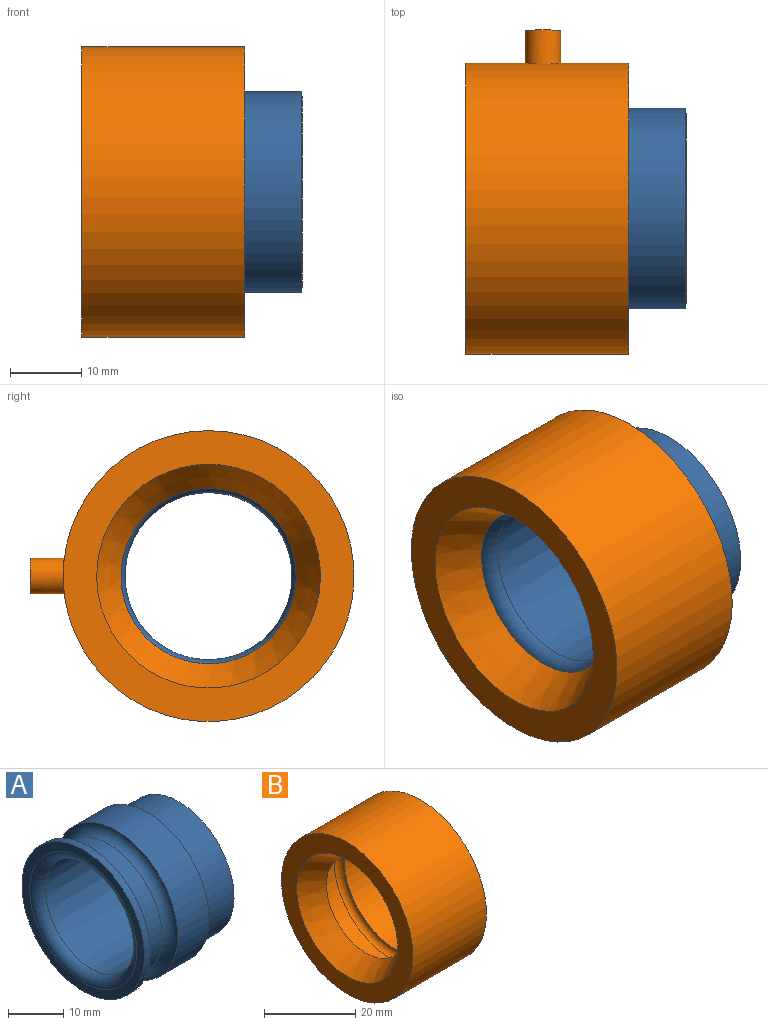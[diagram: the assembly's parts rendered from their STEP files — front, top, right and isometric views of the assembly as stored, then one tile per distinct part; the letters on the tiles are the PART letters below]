
ASSEMBLY  parts=2 mates=1
PART A: 12 faces, bbox 24.5x37x37 mm
  f0: plane 31.32x31.32mm, normal (-1,0,0), area 181mm2, adj f1,f11
  f1: torus R=13.7mm, axis (-1,0,0), area 248.4mm2, adj f0,f2
  f2: cone r=11.69mm half-angle=0.9deg, axis (1,0,0), area 1677mm2, adj f1,f3
  f3: cone r=12.04mm half-angle=89.1deg, axis (-1,0,0), area 164.6mm2, adj f2,f4
  f4: cylinder r=14.05mm len=28.09mm, axis (-1,0,0), area 706mm2, adj f3,f5
  f5: plane 31.32x31.32mm, normal (1,0,0), area 150.9mm2, adj f4,f6
  f6: cylinder r=15.66mm len=31.32mm, axis (-1,0,0), area 787.3mm2, adj f5,f7
  f7: torus R=15.66mm, axis (-1,0,0), area 284mm2, adj f6,f8
  f8: cylinder r=13.66mm len=27.32mm, axis (-1,0,0), area 343.4mm2, adj f7,f9
  f9: torus R=14.66mm, axis (-1,0,0), area 138.4mm2, adj f8,f10
  f10: plane 31.32x31.32mm, normal (1,0,0), area 95.3mm2, adj f9,f11
  f11: cylinder r=15.66mm len=31.32mm, axis (-1,0,0), area 147.6mm2, adj f0,f10
PART B: 13 faces, bbox 22.8x45.4x40.7 mm
  f0: cylinder r=17.37mm len=34.74mm, axis (-1,0,0), area 645.2mm2, adj f1,f9,f10
  f1: torus R=15.87mm, axis (-1,0,0), area 249.1mm2, adj f0,f2
  f2: plane 31.74x31.74mm, normal (-1,0,0), area 20.4mm2, adj f1,f3
  f3: cylinder r=15.66mm len=31.32mm, axis (-1,0,0), area 787.3mm2, adj f2,f4
  f4: plane 40.74x40.74mm, normal (1,0,0), area 532.7mm2, adj f3,f5
  f5: cylinder r=20.37mm len=40.74mm, axis (-1,0,0), area 2899.8mm2, adj f4,f6,f11
  f6: plane 40.74x40.74mm, normal (-1,0,0), area 532.7mm2, adj f5,f7
  f7: cone r=15.66mm half-angle=30.3deg, axis (-1,0,0), area 590.6mm2, adj f6,f8
  f8: plane 31.74x31.74mm, normal (1,0,0), area 318.3mm2, adj f7,f9
  f9: torus R=15.87mm, axis (-1,0,0), area 249.1mm2, adj f0,f8
  f10: cylinder r=1.75mm len=7.72mm, axis (0,-1,0), area 84.4mm2, adj f0,f12
  f11: cylinder r=2.5mm len=5mm, axis (0,-1,0), area 74mm2, adj f5,f12
  f12: plane 5x5mm, normal (0,1,0), area 10mm2, adj f10,f11
PLACE A t=(75.57,13.4,0)mm
PLACE B t=(75.57,13.4,0)mm
MATE fastened B.f0 <-> A.f1  axis (1,0,0) through (76.88,13.4,0)mm
